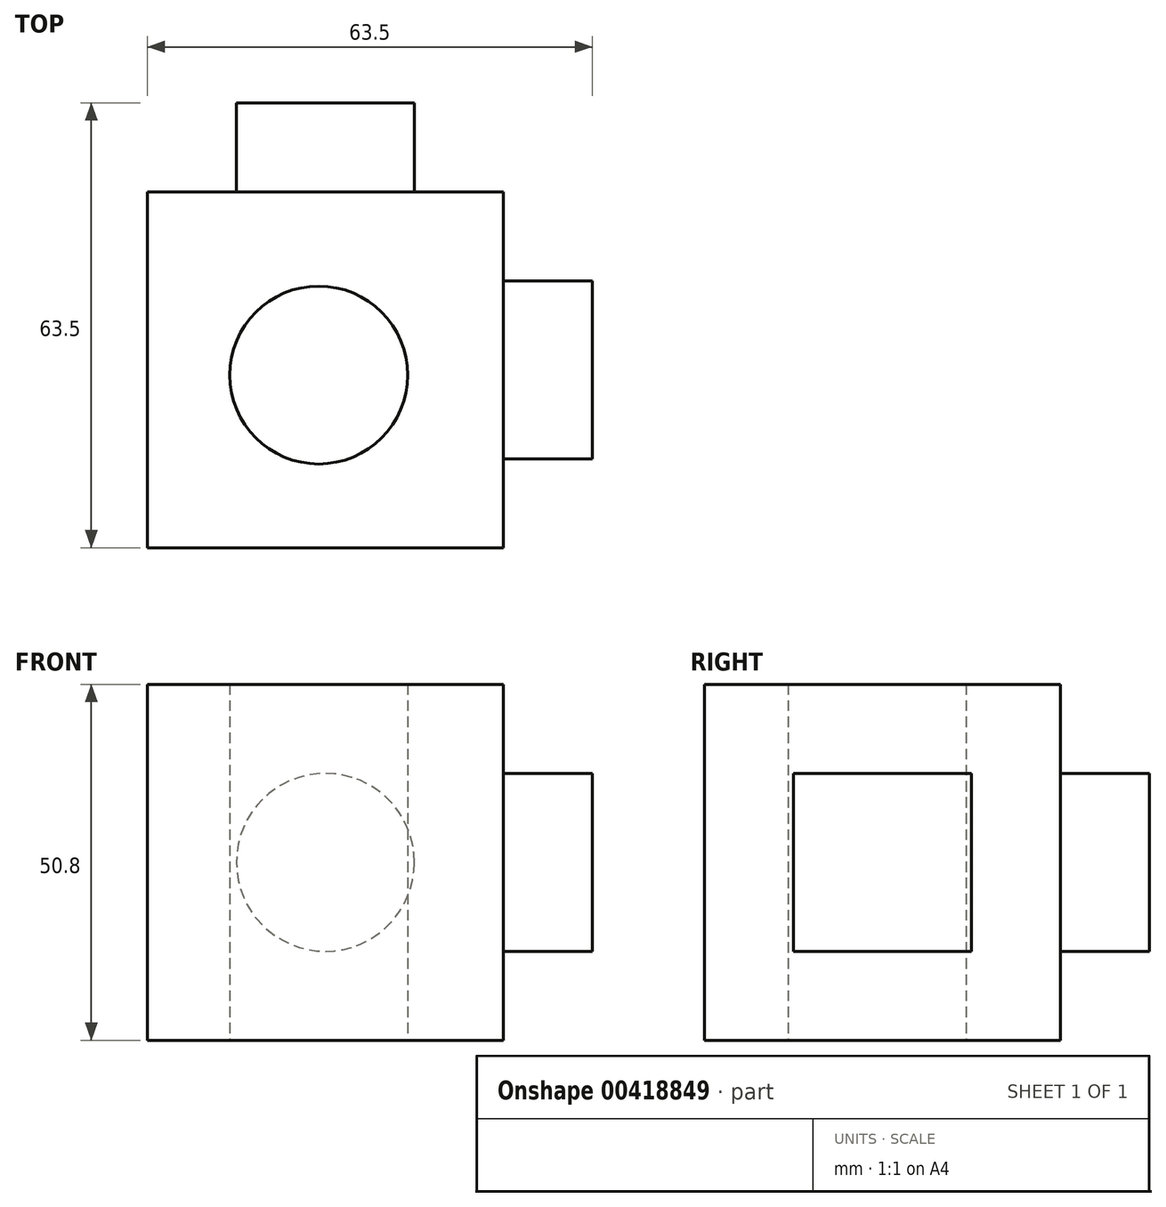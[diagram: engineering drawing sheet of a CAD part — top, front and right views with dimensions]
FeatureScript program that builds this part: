
annotation { "Feature Type Name" : "Feature", "Feature Type Description" : "" }
export const myFeature = defineFeature(function(context is Context, id is Id, definition is map)
    precondition{}
    {
        {
            var Q0;
            Q0=qCreatedBy(makeId("Front.planeOp"),FACE);
            var sketch = newSketch(context, id + "F0", { "sketchPlane" : qUnion([Q0])});
            skLineSegment(sketch, "E0.bottom", {"start": v(0, 0) * mm, "end": v(-50.8, 0) * mm});
            skLineSegment(sketch, "E0.top", {"start": v(0, 50.8) * mm, "end": v(-50.8, 50.8) * mm});
            skLineSegment(sketch, "E0.left", {"start": v(0, 0) * mm, "end": v(0, 50.8) * mm});
            skLineSegment(sketch, "E0.right", {"start": v(-50.8, 0) * mm, "end": v(-50.8, 50.8) * mm});
            skSolve(sketch);
        }
        {
            var Q0;
            Q0 = qSketchRegion(id + "F0", true);
            extrude(context, id + "F1", {"entities" : qUnion([Q0]), "depth" : 50.8 * mm});
        }
        {
            var Q0;
            Q0=qCreatedBy(makeId("Front.planeOp"),FACE);
            var sketch = newSketch(context, id + "F2", { "sketchPlane" : qUnion([Q0])});
            skCircle(sketch, "E1", {"center": v(-25.4, 25.4) * mm, "radius": 12.7 * mm});
            skSolve(sketch);
        }
        {
            var Q0;
            Q0 = qSketchRegion(id + "F2", true);
            extrude(context, id + "F3", {"entities" : qUnion([Q0]), "operationType" : NewBodyOperationType.ADD, "oppositeDirection" : true, "depth" : 12.7 * mm});
        }
        {
            var Q0;
            Q0=qCreatedBy(makeId("Right.planeOp"),FACE);
            var sketch = newSketch(context, id + "F4", { "sketchPlane" : qUnion([Q0])});
            skLineSegment(sketch, "E2.bottom", {"start": v(-38.1, 38.1) * mm, "end": v(-12.7, 38.1) * mm});
            skLineSegment(sketch, "E2.top", {"start": v(-38.1, 12.7) * mm, "end": v(-12.7, 12.7) * mm});
            skLineSegment(sketch, "E2.left", {"start": v(-38.1, 38.1) * mm, "end": v(-38.1, 12.7) * mm});
            skLineSegment(sketch, "E2.right", {"start": v(-12.7, 38.1) * mm, "end": v(-12.7, 12.7) * mm});
            skSolve(sketch);
        }
        {
            var Q0;
            Q0 = qSketchRegion(id + "F4", true);
            extrude(context, id + "F5", {"entities" : qUnion([Q0]), "operationType" : NewBodyOperationType.ADD, "depth" : 12.7 * mm});
        }
        {
            var Q0;
            Q0=qCreatedBy(makeId("Top.planeOp"),FACE);
            var sketch = newSketch(context, id + "F6", { "sketchPlane" : qUnion([Q0])});
            skCircle(sketch, "E3", {"center": v(-26.35, -26.16) * mm, "radius": 12.7 * mm});
            skSolve(sketch);
        }
        {
            var Q0;
            Q0=makeQuery(id+"F6.imprint","IMPRINT",FACE,{"disambiguationData":[TD([[makeQuery(id+"F6.imprint","IMPRINT",EDGE,{"derivedFrom":sQuery(id+"F6.wireOp",EDGE,"E3")}),1.0]])]});
            extrude(context, id + "F7", {"entities" : qUnion([Q0]), "operationType" : NewBodyOperationType.REMOVE, "depth" : 50.8 * mm});
        }
    });
